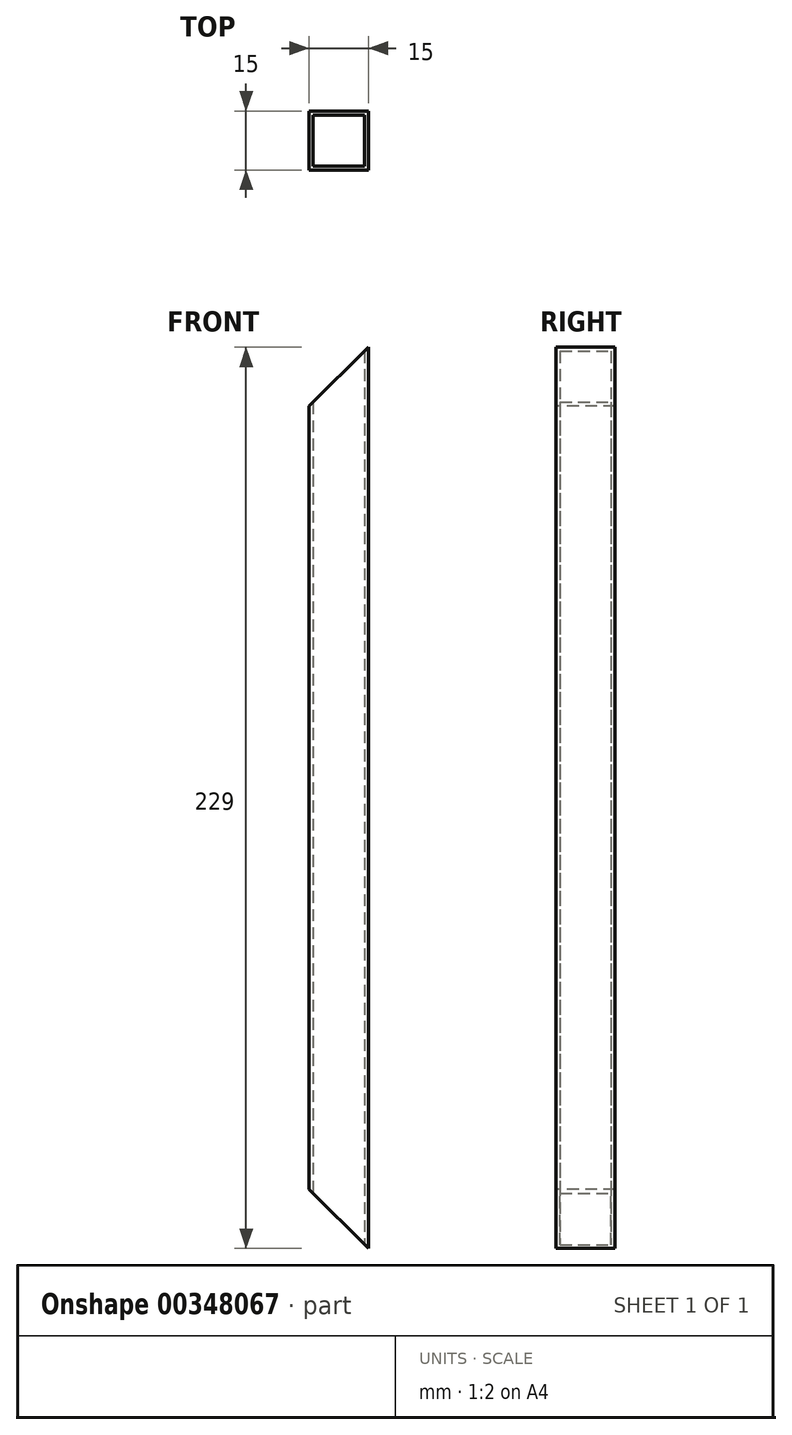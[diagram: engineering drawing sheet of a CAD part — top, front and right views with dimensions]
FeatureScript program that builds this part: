
annotation { "Feature Type Name" : "Feature", "Feature Type Description" : "" }
export const myFeature = defineFeature(function(context is Context, id is Id, definition is map)
    precondition{}
    {
        {
            assignVariable(context, id + "F0", {"name" : "BarLength", "anyValue" : 229});
        }
        {
            var Q0;
            Q0=qCreatedBy(makeId("Top.planeOp"),FACE);
            var sketch = newSketch(context, id + "F1", { "sketchPlane" : qUnion([Q0])});
            skLineSegment(sketch, "E0.bottom", {"start": v(-7.5, 7.5) * mm, "end": v(7.5, 7.5) * mm});
            skLineSegment(sketch, "E0.top", {"start": v(-7.5, -7.5) * mm, "end": v(7.5, -7.5) * mm});
            skLineSegment(sketch, "E0.left", {"start": v(-7.5, 7.5) * mm, "end": v(-7.5, -7.5) * mm});
            skLineSegment(sketch, "E0.right", {"start": v(7.5, 7.5) * mm, "end": v(7.5, -7.5) * mm});
            skPoint(sketch, "E0.middle", {"position": v(0, 0) * mm});
            skLineSegment(sketch, "E1.bottom", {"start": v(-6.5, 6.5) * mm, "end": v(6.5, 6.5) * mm});
            skLineSegment(sketch, "E1.top", {"start": v(-6.5, -6.5) * mm, "end": v(6.5, -6.5) * mm});
            skLineSegment(sketch, "E1.left", {"start": v(-6.5, 6.5) * mm, "end": v(-6.5, -6.5) * mm});
            skLineSegment(sketch, "E1.right", {"start": v(6.5, 6.5) * mm, "end": v(6.5, -6.5) * mm});
            skSolve(sketch);
        }
        {
            var Q0;
            Q0=makeQuery(id+"F1.imprint","IMPRINT",FACE,{"disambiguationData":[TD([[makeQuery(id+"F1.imprint","IMPRINT",EDGE,{"derivedFrom":sQuery(id+"F1.wireOp",EDGE,"E0.bottom")}),-1.0]])]});
            extrude(context, id + "F2", {"entities" : qUnion([Q0]), "depth" : (getVariable(context, 'BarLength')) * mm});
        }
        {
            var Q0;
            Q0=makeQuery(id+"F2.opExtrude","SWEPT_FACE",FACE,{"disambiguationData":[OSD([sQuery(id+"F1.wireOp",EDGE,"E0.top")])]});
            var sketch = newSketch(context, id + "F3", { "sketchPlane" : qUnion([Q0])});
            skLineSegment(sketch, "E2", {"start": v(-7.5, 229) * mm, "end": v(7.5, 229) * mm});
            skLineSegment(sketch, "E3", {"start": v(-7.5, 0) * mm, "end": v(7.5, 0) * mm});
            skLineSegment(sketch, "E4", {"start": v(7.5, 0) * mm, "end": v(7.5, 14.26) * mm});
            skLineSegment(sketch, "E5", {"start": v(-7.5, 229) * mm, "end": v(-7.5, 214) * mm});
            skLineSegment(sketch, "E6", {"start": v(-7.5, 214) * mm, "end": v(7.5, 229) * mm});
            skLineSegment(sketch, "E7", {"start": v(-7.5, 0) * mm, "end": v(-7.5, 15) * mm});
            skLineSegment(sketch, "E8", {"start": v(-7.5, 15) * mm, "end": v(7.5, 0) * mm});
            skSolve(sketch);
        }
        {
            var Q0;
            Q0=makeQuery(id+"F3.imprint","IMPRINT",FACE,{"disambiguationData":[TD([[makeQuery(id+"F3.imprint","IMPRINT",EDGE,{"derivedFrom":sQuery(id+"F3.wireOp",EDGE,"E3")}),1.0]])]});
            var Q1;
            Q1=makeQuery(id+"F3.imprint","IMPRINT",FACE,{"disambiguationData":[TD([[makeQuery(id+"F3.imprint","IMPRINT",EDGE,{"derivedFrom":sQuery(id+"F3.wireOp",EDGE,"E2")}),-1.0]])]});
            var Q2;
            Q2=makeQuery(id+"F3.imprint","IMPRINT",FACE,{"disambiguationData":[TD([[makeQuery(id+"F3.imprint","IMPRINT",EDGE,{"derivedFrom":sQuery(id+"F3.wireOp",EDGE,"E7")}),1.0]])]});
            extrude(context, id + "F4", {"entities" : qUnion([Q0, Q1, Q2]), "operationType" : NewBodyOperationType.REMOVE, "oppositeDirection" : true, "depth" : 25 * mm});
        }
    });
